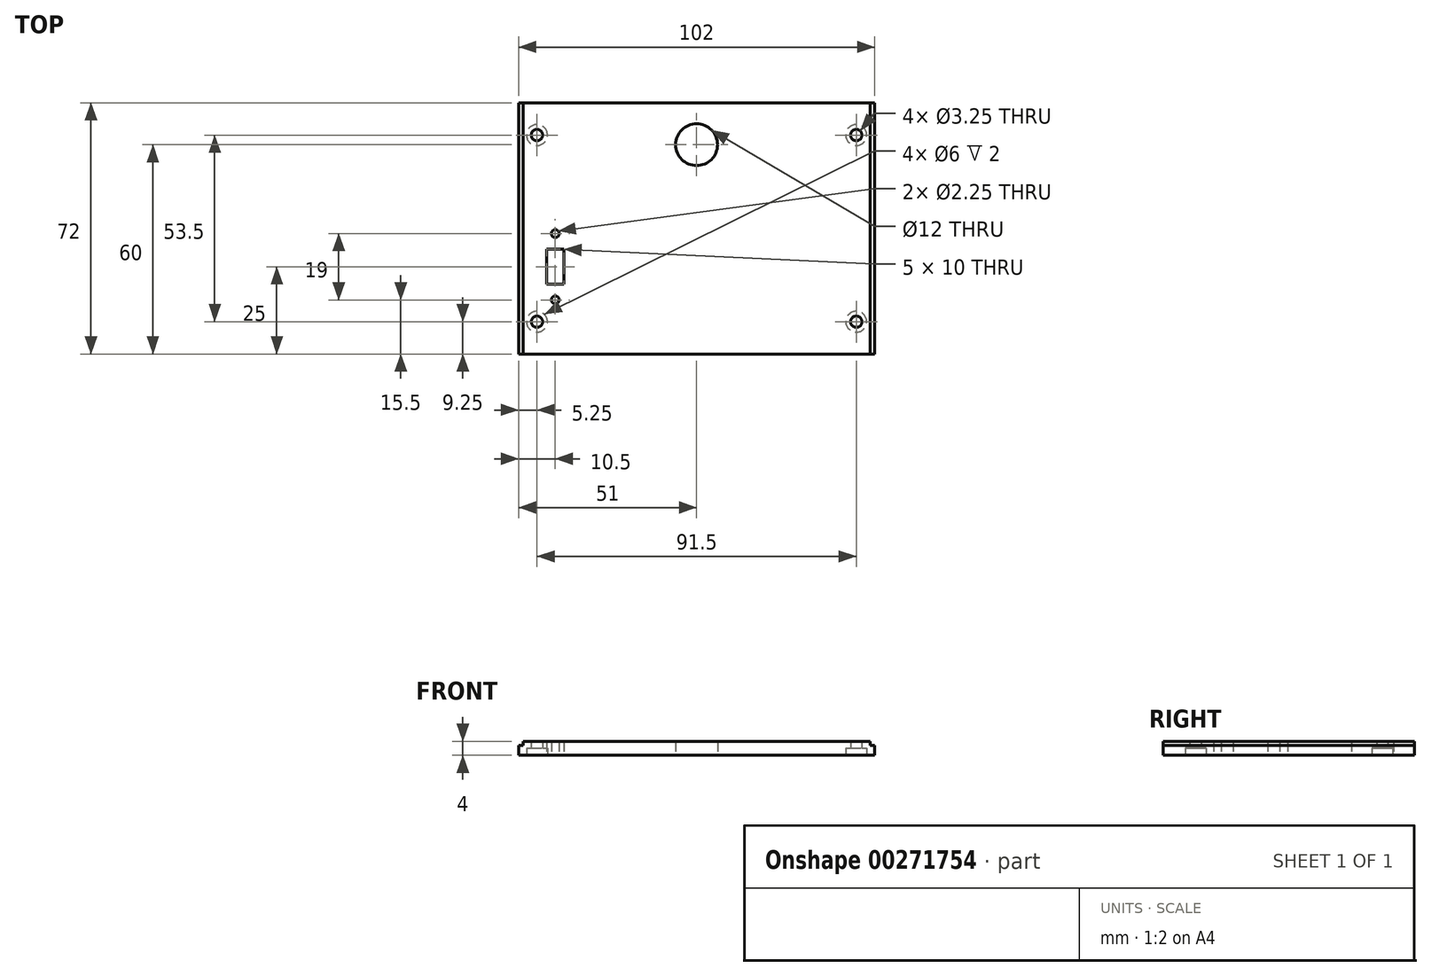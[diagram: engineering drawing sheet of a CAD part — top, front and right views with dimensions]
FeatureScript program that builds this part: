
annotation { "Feature Type Name" : "Feature", "Feature Type Description" : "" }
export const myFeature = defineFeature(function(context is Context, id is Id, definition is map)
    precondition{}
    {
        {
            var Q0;
            Q0=qCreatedBy(makeId("Top.planeOp"),FACE);
            var sketch = newSketch(context, id + "F0", { "sketchPlane" : qUnion([Q0])});
            skLineSegment(sketch, "E0.bottom", {"start": v(-51, 36) * mm, "end": v(51, 36) * mm});
            skLineSegment(sketch, "E0.top", {"start": v(-51, -36) * mm, "end": v(51, -36) * mm});
            skLineSegment(sketch, "E0.left", {"start": v(-51, 36) * mm, "end": v(-51, -36) * mm});
            skLineSegment(sketch, "E0.right", {"start": v(51, 36) * mm, "end": v(51, -36) * mm});
            skSolve(sketch);
        }
        {
            var Q0;
            Q0 = qSketchRegion(id + "F0", true);
            extrude(context, id + "F1", {"entities" : qUnion([Q0]), "depth" : 2.75 * mm});
        }
        {
            var Q0;
            Q0=makeQuery(id+"F1.opExtrude","CAP_FACE",FACE,{"disambiguationData":[OSD([sQuery(id+"F0.wireOp",EDGE,"E0.bottom"),sQuery(id+"F0.wireOp",EDGE,"E0.top"),sQuery(id+"F0.wireOp",EDGE,"E0.left"),sQuery(id+"F0.wireOp",EDGE,"E0.right")])],"isStart":false});
            var sketch = newSketch(context, id + "F2", { "sketchPlane" : qUnion([Q0])});
            skLineSegment(sketch, "E1.bottom", {"start": v(-49.75, 36) * mm, "end": v(49.75, 36) * mm});
            skLineSegment(sketch, "E1.top", {"start": v(-49.75, -36) * mm, "end": v(49.75, -36) * mm});
            skLineSegment(sketch, "E1.left", {"start": v(-49.75, 36) * mm, "end": v(-49.75, -36) * mm});
            skLineSegment(sketch, "E1.right", {"start": v(49.75, 36) * mm, "end": v(49.75, -36) * mm});
            skSolve(sketch);
        }
        {
            var Q0;
            Q0 = qSketchRegion(id + "F2", true);
            extrude(context, id + "F3", {"entities" : qUnion([Q0]), "operationType" : NewBodyOperationType.ADD, "depth" : 1.25 * mm});
        }
        {
            var Q0;
            Q0=makeQuery(id+"F1.opExtrude","CAP_FACE",FACE,{"disambiguationData":[OSD([sQuery(id+"F0.wireOp",EDGE,"E0.bottom"),sQuery(id+"F0.wireOp",EDGE,"E0.top"),sQuery(id+"F0.wireOp",EDGE,"E0.left"),sQuery(id+"F0.wireOp",EDGE,"E0.right")])],"isStart":true});
            var sketch = newSketch(context, id + "F4", { "sketchPlane" : qUnion([Q0])});
            skPoint(sketch, "E2", {"position": v(-45.75, -26.75) * mm});
            skPoint(sketch, "E3", {"position": v(45.75, -26.75) * mm});
            skPoint(sketch, "E4", {"position": v(-45.75, 26.75) * mm});
            skPoint(sketch, "E5", {"position": v(45.75, 26.75) * mm});
            skSolve(sketch);
        }
        {
            var Q0;
            Q0=sQuery(id+"F4.wireOp",VERTEX,"E4");
            var Q1;
            Q1=sQuery(id+"F4.wireOp",VERTEX,"E5");
            var Q2;
            Q2=sQuery(id+"F4.wireOp",VERTEX,"E3");
            var Q3;
            Q3=sQuery(id+"F4.wireOp",VERTEX,"E2");
            var Q4;
            Q4=makeQuery(id+"F1.opExtrude","SWEPT_BODY",BODY,{"disambiguationData":[OSD([sQuery(id+"F0.wireOp",EDGE,"E0.bottom"),sQuery(id+"F0.wireOp",EDGE,"E0.top"),sQuery(id+"F0.wireOp",EDGE,"E0.left"),sQuery(id+"F0.wireOp",EDGE,"E0.right")])]});
            hole(context, id + "F5", {"style" : HoleStyle.C_BORE, "endStyle" : HoleEndStyle.BLIND, "holeDiameter" : 3.25 * mm, "cBoreDiameter" : 6 * mm, "cBoreDepth" : 2 * mm, "holeDepth" : 8 * mm, "tappedDepth" : 12 * mm, "tapClearance" : 3, "startFromSketch" : true, "locations" : qUnion([Q0, Q1, Q2, Q3]), "scope" : qUnion([Q4])});
        }
        {
            var Q0;
            Q0=makeQuery(id+"F1.opExtrude","CAP_FACE",FACE,{"disambiguationData":[OSD([sQuery(id+"F0.wireOp",EDGE,"E0.bottom"),sQuery(id+"F0.wireOp",EDGE,"E0.top"),sQuery(id+"F0.wireOp",EDGE,"E0.left"),sQuery(id+"F0.wireOp",EDGE,"E0.right")])],"isStart":true});
            var sketch = newSketch(context, id + "F6", { "sketchPlane" : qUnion([Q0])});
            skLineSegment(sketch, "E6.bottom", {"start": v(-43, 16) * mm, "end": v(-38, 16) * mm});
            skLineSegment(sketch, "E6.top", {"start": v(-43, 6) * mm, "end": v(-38, 6) * mm});
            skLineSegment(sketch, "E6.left", {"start": v(-43, 16) * mm, "end": v(-43, 6) * mm});
            skLineSegment(sketch, "E6.right", {"start": v(-38, 16) * mm, "end": v(-38, 6) * mm});
            skLineSegment(sketch, "E7", {"start": v(-40.5, 16) * mm, "end": v(-40.5, 20.9) * mm});
            skLineSegment(sketch, "E8", {"start": v(-40.5, 6) * mm, "end": v(-40.5, 1.1) * mm});
            skPoint(sketch, "E9", {"position": v(-40.5, 20.9) * mm});
            skPoint(sketch, "E10", {"position": v(-40.5, 1.1) * mm});
            skLineSegment(sketch, "E11", {"start": v(-38, 11) * mm, "end": v(-27.92, 11) * mm});
            skSolve(sketch);
        }
        {
            var Q0;
            Q0 = qSketchRegion(id + "F6", true);
            extrude(context, id + "F7", {"entities" : qUnion([Q0]), "operationType" : NewBodyOperationType.REMOVE, "oppositeDirection" : true, "depth" : 4 * mm});
        }
        {
            var Q0;
            Q0=makeQuery(id+"F1.opExtrude","CAP_FACE",FACE,{"disambiguationData":[OSD([sQuery(id+"F0.wireOp",EDGE,"E0.bottom"),sQuery(id+"F0.wireOp",EDGE,"E0.top"),sQuery(id+"F0.wireOp",EDGE,"E0.left"),sQuery(id+"F0.wireOp",EDGE,"E0.right")])],"isStart":true});
            var sketch = newSketch(context, id + "F8", { "sketchPlane" : qUnion([Q0])});
            skLineSegment(sketch, "E12", {"start": v(-40.5, 16) * mm, "end": v(-40.5, 20.5) * mm});
            skLineSegment(sketch, "E13", {"start": v(-40.5, 6) * mm, "end": v(-40.5, 1.5) * mm});
            skPoint(sketch, "E14", {"position": v(-40.5, 20.5) * mm});
            skPoint(sketch, "E15", {"position": v(-40.5, 1.5) * mm});
            skSolve(sketch);
        }
        {
            var Q0;
            Q0=sQuery(id+"F8.wireOp",VERTEX,"E14");
            var Q1;
            Q1=sQuery(id+"F8.wireOp",VERTEX,"E15");
            var Q2;
            Q2=makeQuery(id+"F1.opExtrude","SWEPT_BODY",BODY,{"disambiguationData":[OSD([sQuery(id+"F0.wireOp",EDGE,"E0.bottom"),sQuery(id+"F0.wireOp",EDGE,"E0.top"),sQuery(id+"F0.wireOp",EDGE,"E0.left"),sQuery(id+"F0.wireOp",EDGE,"E0.right")])]});
            hole(context, id + "F9", {"style" : HoleStyle.SIMPLE, "endStyle" : HoleEndStyle.THROUGH, "holeDiameter" : 2.25 * mm, "tappedDepth" : 12 * mm, "tapClearance" : 3, "startFromSketch" : true, "locations" : qUnion([Q0, Q1]), "scope" : qUnion([Q2])});
        }
        {
            var Q0;
            Q0=makeQuery(id+"F1.opExtrude","CAP_FACE",FACE,{"disambiguationData":[OSD([sQuery(id+"F0.wireOp",EDGE,"E0.bottom"),sQuery(id+"F0.wireOp",EDGE,"E0.top"),sQuery(id+"F0.wireOp",EDGE,"E0.left"),sQuery(id+"F0.wireOp",EDGE,"E0.right")])],"isStart":true});
            var sketch = newSketch(context, id + "F10", { "sketchPlane" : qUnion([Q0])});
            skPoint(sketch, "E16", {"position": v(0, -24) * mm});
            skSolve(sketch);
        }
        {
            var Q0;
            Q0=sQuery(id+"F10.wireOp",VERTEX,"E16");
            var Q1;
            Q1=makeQuery(id+"F1.opExtrude","SWEPT_BODY",BODY,{"disambiguationData":[OSD([sQuery(id+"F0.wireOp",EDGE,"E0.bottom"),sQuery(id+"F0.wireOp",EDGE,"E0.top"),sQuery(id+"F0.wireOp",EDGE,"E0.left"),sQuery(id+"F0.wireOp",EDGE,"E0.right")])]});
            hole(context, id + "F11", {"style" : HoleStyle.SIMPLE, "endStyle" : HoleEndStyle.THROUGH, "holeDiameter" : 12 * mm, "tappedDepth" : 12 * mm, "tapClearance" : 3, "startFromSketch" : true, "locations" : qUnion([Q0]), "scope" : qUnion([Q1])});
        }
    });
